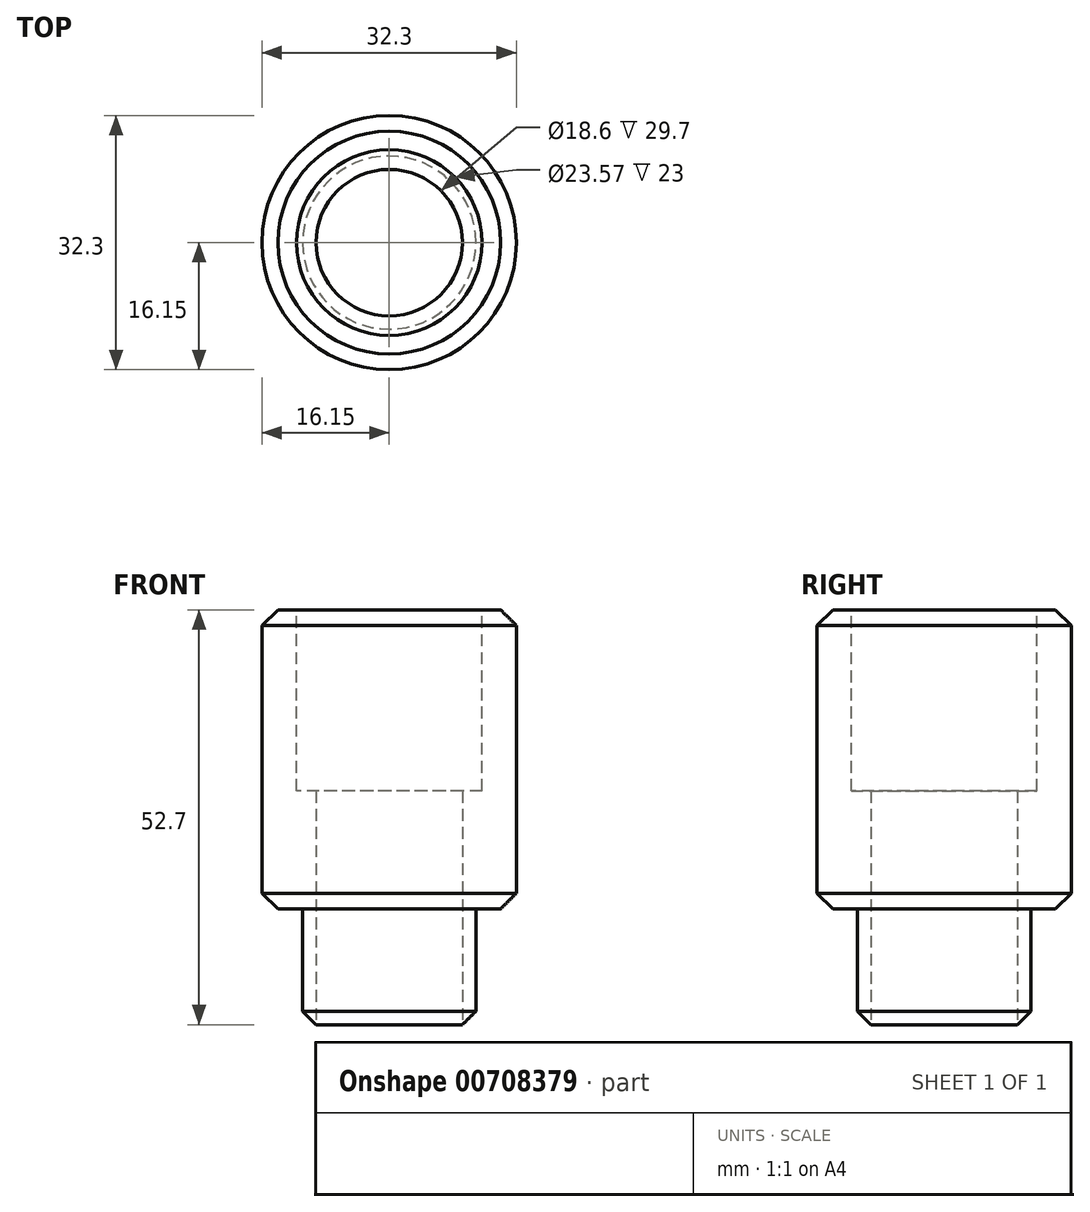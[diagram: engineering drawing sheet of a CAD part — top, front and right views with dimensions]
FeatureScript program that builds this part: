
annotation { "Feature Type Name" : "Feature", "Feature Type Description" : "" }
export const myFeature = defineFeature(function(context is Context, id is Id, definition is map)
    precondition{}
    {
        {
            var Q0;
            Q0=qCreatedBy(makeId("Top.planeOp"),FACE);
            var sketch = newSketch(context, id + "F0", { "sketchPlane" : qUnion([Q0])});
            skCircle(sketch, "E0", {"center": v(0, 0) * mm, "radius": 11 * mm});
            skSolve(sketch);
        }
        {
            var Q0;
            Q0=qSketchRegion(id+"F0",true);
            extrude(context, id + "F1", {"entities" : qUnion([Q0]), "depth" : 15 * mm, "offsetDistance" : 25 * mm});
        }
        {
            var Q0;
            Q0=makeQuery(id+"F1.opExtrude","CAP_FACE",FACE,{"disambiguationData":[OSD([sQuery(id+"F0.wireOp",EDGE,"E0")])],"isStart":false});
            var sketch = newSketch(context, id + "F2", { "sketchPlane" : qUnion([Q0])});
            skCircle(sketch, "E1", {"center": v(0, 0) * mm, "radius": 16.15 * mm});
            skSolve(sketch);
        }
        {
            var Q0;
            Q0=qSketchRegion(id+"F2",true);
            extrude(context, id + "F3", {"entities" : qUnion([Q0]), "operationType" : NewBodyOperationType.ADD, "depth" : 38 * mm, "offsetDistance" : 25 * mm});
        }
        {
            var Q0;
            Q0=makeQuery(id+"F1.opExtrude","CAP_FACE",FACE,{"disambiguationData":[OSD([sQuery(id+"F0.wireOp",EDGE,"E0")])],"isStart":true});
            var sketch = newSketch(context, id + "F4", { "sketchPlane" : qUnion([Q0])});
            skCircle(sketch, "E2", {"center": v(0, 0) * mm, "radius": 9.3 * mm});
            skSolve(sketch);
        }
        {
            var Q0;
            Q0=qSketchRegion(id+"F4",true);
            extrude(context, id + "F5", {"entities" : qUnion([Q0]), "operationType" : NewBodyOperationType.REMOVE, "endBound" : BoundingType.THROUGH_ALL, "oppositeDirection" : true, "depth" : 25 * mm, "offsetDistance" : 25 * mm});
        }
        {
            var Q0;
            Q0=qCreatedBy(makeId("Top.planeOp"),FACE);
            cPlane(context, id + "F6", {"entities" : qUnion([Q0]), "cplaneType" : CPlaneType.OFFSET, "offset" : 55 * mm, "width" : 150 * mm, "height" : 150 * mm});
        }
        {
            var Q0;
            Q0=qCreatedBy(id+"F6.planeOp",FACE);
            var sketch = newSketch(context, id + "F7", { "sketchPlane" : qUnion([Q0])});
            skCircle(sketch, "E3", {"center": v(0, 0) * mm, "radius": 11.78 * mm});
            skSolve(sketch);
        }
        {
            var Q0;
            Q0=makeQuery(id+"F7.imprint","IMPRINT",FACE,{"disambiguationData":[TD([[makeQuery(id+"F7.imprint","IMPRINT",EDGE,{"derivedFrom":sQuery(id+"F7.wireOp",EDGE,"E3")}),1.0]])]});
            var Q1;
            Q1=sQuery(id+"F7.wireOp",EDGE,"E3");
            extrude(context, id + "F8", {"entities" : qUnion([Q0]), "operationType" : NewBodyOperationType.REMOVE, "surfaceEntities" : qUnion([Q1]), "oppositeDirection" : true, "depth" : 25 * mm, "offsetDistance" : 25 * mm});
        }
        {
            var Q0;
            Q0=makeQuery(id+"F3.opExtrude","CAP_EDGE",EDGE,{"disambiguationData":[OSD([sQuery(id+"F2.wireOp",EDGE,"E1")])],"isStart":false});
            var Q1;
            Q1=makeQuery(id+"F1.opExtrude","CAP_EDGE",EDGE,{"disambiguationData":[OSD([sQuery(id+"F0.wireOp",EDGE,"E0")])],"isStart":true});
            var Q2;
            Q2=makeQuery(id+"F3.opExtrude","CAP_EDGE",EDGE,{"disambiguationData":[OSD([sQuery(id+"F2.wireOp",EDGE,"E1")])],"isStart":true});
            chamfer(context, id + "F9", {"entities" : qUnion([Q0, Q1, Q2]), "width" : 2 * mm, "tangentPropagation" : true});
        }
    });
